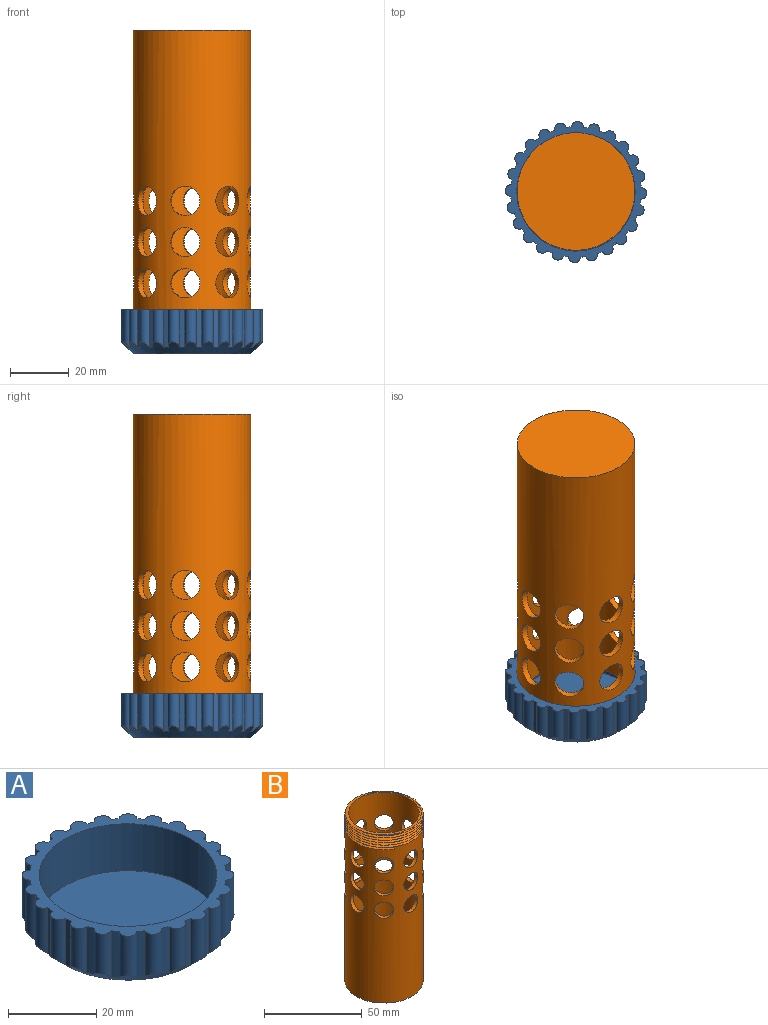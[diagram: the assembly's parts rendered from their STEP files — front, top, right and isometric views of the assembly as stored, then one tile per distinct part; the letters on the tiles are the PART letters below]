
ASSEMBLY  parts=2 mates=1
PART A: 53 faces, bbox 48x48x15 mm
  f0: cylinder r=22.2mm len=12.8mm, axis (0,0,-1), area 23.2mm2, adj f46,f47,f48,f50
  f1: cylinder r=22.2mm len=12.8mm, axis (0,0,-1), area 23.2mm2, adj f24,f47,f48,f50
  f2: cylinder r=22.2mm len=12.8mm, axis (0,0,-1), area 23.2mm2, adj f45,f46,f48,f50
  f3: cylinder r=22.2mm len=12.8mm, axis (0,0,-1), area 23.2mm2, adj f44,f45,f48,f50
  f4: cylinder r=22.2mm len=12.8mm, axis (0,0,-1), area 23.2mm2, adj f43,f44,f48,f50
  f5: cylinder r=22.2mm len=12.8mm, axis (0,0,-1), area 23.2mm2, adj f42,f43,f48,f50
  f6: cylinder r=22.2mm len=12.8mm, axis (0,0,-1), area 23.2mm2, adj f41,f42,f48,f50
  f7: cylinder r=22.2mm len=12.8mm, axis (0,0,-1), area 23.2mm2, adj f40,f41,f48,f50
  f8: cylinder r=22.2mm len=12.8mm, axis (0,0,-1), area 23.2mm2, adj f39,f40,f48,f50
  f9: cylinder r=22.2mm len=12.8mm, axis (0,0,-1), area 23.2mm2, adj f38,f39,f48,f50
  f10: cylinder r=22.2mm len=12.8mm, axis (0,0,-1), area 23.2mm2, adj f37,f38,f48,f50
  f11: cylinder r=22.2mm len=12.8mm, axis (0,0,-1), area 23.2mm2, adj f36,f37,f48,f50
  f12: cylinder r=22.2mm len=12.8mm, axis (0,0,-1), area 23.2mm2, adj f35,f36,f48,f50
  f13: cylinder r=22.2mm len=12.8mm, axis (0,0,-1), area 23.2mm2, adj f34,f35,f48,f50
  f14: cylinder r=22.2mm len=12.8mm, axis (0,0,-1), area 23.2mm2, adj f33,f34,f48,f50
  f15: cylinder r=22.2mm len=12.8mm, axis (0,0,-1), area 23.2mm2, adj f32,f33,f48,f50
  f16: cylinder r=22.2mm len=12.8mm, axis (0,0,-1), area 23.2mm2, adj f31,f32,f48,f50
  f17: cylinder r=22.2mm len=12.8mm, axis (0,0,-1), area 23.2mm2, adj f30,f31,f48,f50
  f18: cylinder r=22.2mm len=12.8mm, axis (0,0,-1), area 23.2mm2, adj f29,f30,f48,f50
  f19: cylinder r=22.2mm len=12.8mm, axis (0,0,-1), area 23.2mm2, adj f28,f29,f48,f50
  f20: cylinder r=22.2mm len=12.8mm, axis (0,0,-1), area 23.2mm2, adj f27,f28,f48,f50
  f21: cylinder r=22.2mm len=12.8mm, axis (0,0,-1), area 23.2mm2, adj f26,f27,f48,f50
  f22: cylinder r=22.2mm len=12.8mm, axis (0,0,-1), area 23.2mm2, adj f25,f26,f48,f50
  f23: cylinder r=22.2mm len=12.8mm, axis (0,0,-1), area 23.2mm2, adj f24,f25,f48,f50
  f24: cylinder r=2mm len=12.8mm, axis (0,0,-1), area 70.6mm2, adj f1,f23,f48,f50
  f25: cylinder r=2mm len=12.8mm, axis (0,0,-1), area 70.6mm2, adj f22,f23,f48,f50
  f26: cylinder r=2mm len=12.8mm, axis (0,0,-1), area 70.6mm2, adj f21,f22,f48,f50
  f27: cylinder r=2mm len=12.8mm, axis (0,0,-1), area 70.6mm2, adj f20,f21,f48,f50
  f28: cylinder r=2mm len=12.8mm, axis (0,0,-1), area 70.6mm2, adj f19,f20,f48,f50
  f29: cylinder r=2mm len=12.8mm, axis (0,0,-1), area 70.6mm2, adj f18,f19,f48,f50
  f30: cylinder r=2mm len=12.8mm, axis (0,0,-1), area 70.6mm2, adj f17,f18,f48,f50
  f31: cylinder r=2mm len=12.8mm, axis (0,0,-1), area 70.6mm2, adj f16,f17,f48,f50
  f32: cylinder r=2mm len=12.8mm, axis (0,0,-1), area 70.6mm2, adj f15,f16,f48,f50
  f33: cylinder r=2mm len=12.8mm, axis (0,0,-1), area 70.6mm2, adj f14,f15,f48,f50
  f34: cylinder r=2mm len=12.8mm, axis (0,0,-1), area 70.6mm2, adj f13,f14,f48,f50
  f35: cylinder r=2mm len=12.8mm, axis (0,0,-1), area 70.6mm2, adj f12,f13,f48,f50
  f36: cylinder r=2mm len=12.8mm, axis (0,0,-1), area 70.6mm2, adj f11,f12,f48,f50
  f37: cylinder r=2mm len=12.8mm, axis (0,0,-1), area 70.6mm2, adj f10,f11,f48,f50
  f38: cylinder r=2mm len=12.8mm, axis (0,0,-1), area 70.6mm2, adj f9,f10,f48,f50
  f39: cylinder r=2mm len=12.8mm, axis (0,0,-1), area 70.6mm2, adj f8,f9,f48,f50
  f40: cylinder r=2mm len=12.8mm, axis (0,0,-1), area 70.6mm2, adj f7,f8,f48,f50
  f41: cylinder r=2mm len=12.8mm, axis (0,0,-1), area 70.6mm2, adj f6,f7,f48,f50
  f42: cylinder r=2mm len=12.8mm, axis (0,0,-1), area 70.6mm2, adj f5,f6,f48,f50
  f43: cylinder r=2mm len=12.8mm, axis (0,0,-1), area 70.6mm2, adj f4,f5,f48,f50
  f44: cylinder r=2mm len=12.8mm, axis (0,0,-1), area 70.6mm2, adj f3,f4,f48,f50
  f45: cylinder r=2mm len=12.8mm, axis (0,0,-1), area 70.6mm2, adj f2,f3,f48,f50
  f46: cylinder r=2mm len=12.8mm, axis (0,0,-1), area 70.6mm2, adj f0,f2,f48,f50
  f47: cylinder r=2mm len=12.8mm, axis (0,0,-1), area 70.6mm2, adj f0,f1,f48,f50
  f48: cone r=20mm half-angle=45deg, axis (0,0,1), area 602.9mm2, adj f0,f1,f2,f3,f4,f5,f6,f7
  f49: plane 40x40mm, normal (0,0,-1), area 1256.6mm2, adj f48
  f50: plane 48x48mm, normal (0,0,1), area 413.6mm2, adj f0,f1,f2,f3,f4,f5,f6,f7
  f51: plane 40.2x40.2mm, normal (0,0,1), area 1269.2mm2, adj f52
  f52: cylinder r=20.1mm len=40.2mm, axis (0,0,-1), area 1641.8mm2, adj f50,f51
PART B: 38 faces, bbox 41.3x47.5x107.3 mm
  f0: cylinder r=20mm len=97.5mm, axis (0,0,-1), area 10226.3mm2, adj f1,f9,f11,f12,f13,f14,f15,f16
  f1: cylinder r=20mm len=40mm, axis (0,0,-1), area 6.3mm2, adj f0,f2,f36,f37
  f2: cylinder r=20mm len=40mm, axis (0,0,-1), area 6.3mm2, adj f1,f3,f36,f37
  f3: cylinder r=20mm len=40mm, axis (0,0,-1), area 6.3mm2, adj f2,f4,f36,f37
  f4: cylinder r=20mm len=40mm, axis (0,0,-1), area 6.2mm2, adj f3,f5,f36,f37
  f5: cylinder r=20mm len=40mm, axis (0,0,-1), area 6.2mm2, adj f4,f6,f36,f37
  f6: cylinder r=20mm len=4.34mm, axis (0,0,-1), area 0.1mm2, adj f5,f8,f37
  f7: cylinder r=18mm len=103mm, axis (0,0,-1), area 9788mm2, adj f8,f10,f11,f12,f13,f14,f15,f16
  f8: plane 40.08x40.07mm, normal (0,0,1), area 164mm2, adj f6,f7,f36,f37
  f9: plane 40x40mm, normal (0,0,-1), area 1256.6mm2, adj f0
  f10: plane 36x36mm, normal (0,0,1), area 1017.9mm2, adj f7
  f11: cylinder r=5mm len=10mm, axis (0,-1,0), area 62.8mm2, adj f0,f7
  f12: cylinder r=5mm len=10mm, axis (0,-1,0), area 62.8mm2, adj f0,f7
  f13: cylinder r=5mm len=10mm, axis (0.71,-0.71,0), area 65.1mm2, adj f0,f7
  f14: cylinder r=5mm len=10mm, axis (0.71,-0.71,0), area 65.1mm2, adj f0,f7
  f15: cylinder r=5mm len=10mm, axis (1,0,0), area 48.4mm2, adj f0,f7
  f16: cylinder r=5mm len=10mm, axis (1,0,0), area 64mm2, adj f0,f7
  f17: cylinder r=5mm len=10mm, axis (0.71,0.71,0), area 65.1mm2, adj f0,f7
  f18: cylinder r=5mm len=10mm, axis (0.71,0.71,0), area 65.1mm2, adj f0,f7
  f19: cylinder r=5mm len=10mm, axis (0,-1,0), area 62.8mm2, adj f0,f7
  f20: cylinder r=5mm len=10mm, axis (0,-1,0), area 62.8mm2, adj f0,f7
  f21: cylinder r=5mm len=10mm, axis (0,-1,0), area 62.8mm2, adj f0,f7
  f22: cylinder r=5mm len=10mm, axis (0,-1,0), area 62.8mm2, adj f0,f7
  f23: cylinder r=5mm len=10mm, axis (0.71,-0.71,0), area 65.1mm2, adj f0,f7
  f24: cylinder r=5mm len=10mm, axis (0.71,-0.71,0), area 65.1mm2, adj f0,f7
  f25: cylinder r=5mm len=10mm, axis (0.71,-0.71,0), area 65.1mm2, adj f0,f7
  f26: cylinder r=5mm len=10mm, axis (0.71,-0.71,0), area 65.1mm2, adj f0,f7
  f27: cylinder r=5mm len=10mm, axis (1,0,0), area 48.4mm2, adj f0,f7
  f28: cylinder r=5mm len=10mm, axis (1,0,0), area 64mm2, adj f0,f7
  f29: cylinder r=5mm len=10mm, axis (1,0,0), area 48.4mm2, adj f0,f7
  f30: cylinder r=5mm len=10mm, axis (1,0,0), area 64mm2, adj f0,f7
  f31: cylinder r=5mm len=10mm, axis (0.71,0.71,0), area 65.1mm2, adj f0,f7
  f32: cylinder r=5mm len=10mm, axis (0.71,0.71,0), area 65.1mm2, adj f0,f7
  f33: cylinder r=5mm len=10mm, axis (0.71,0.71,0), area 65.1mm2, adj f0,f7
  f34: cylinder r=5mm len=10mm, axis (0.71,0.71,0), area 65.1mm2, adj f0,f7
  f35: plane 1.45x1.09mm, normal (-0.87,0.5,0), area 0.9mm2, adj f0,f36,f37
  f36: bspline ~46.19x40mm, area 1046.1mm2, adj f0,f1,f2,f3,f4,f5,f8,f35
  f37: bspline ~46.19x40mm, area 960.4mm2, adj f0,f1,f2,f3,f4,f5,f6,f8
PLACE A rot(axis=(0,0,1),28.8deg) t=(-69.67,58.98,34.98)mm
PLACE B rot(axis=(-1,0.06,0),180deg) t=(-69.67,58.98,144.94)mm
MATE cylindrical A.f0 <-> B.f0  axis (0,0,1) through (-69.67,58.98,49.98)mm
